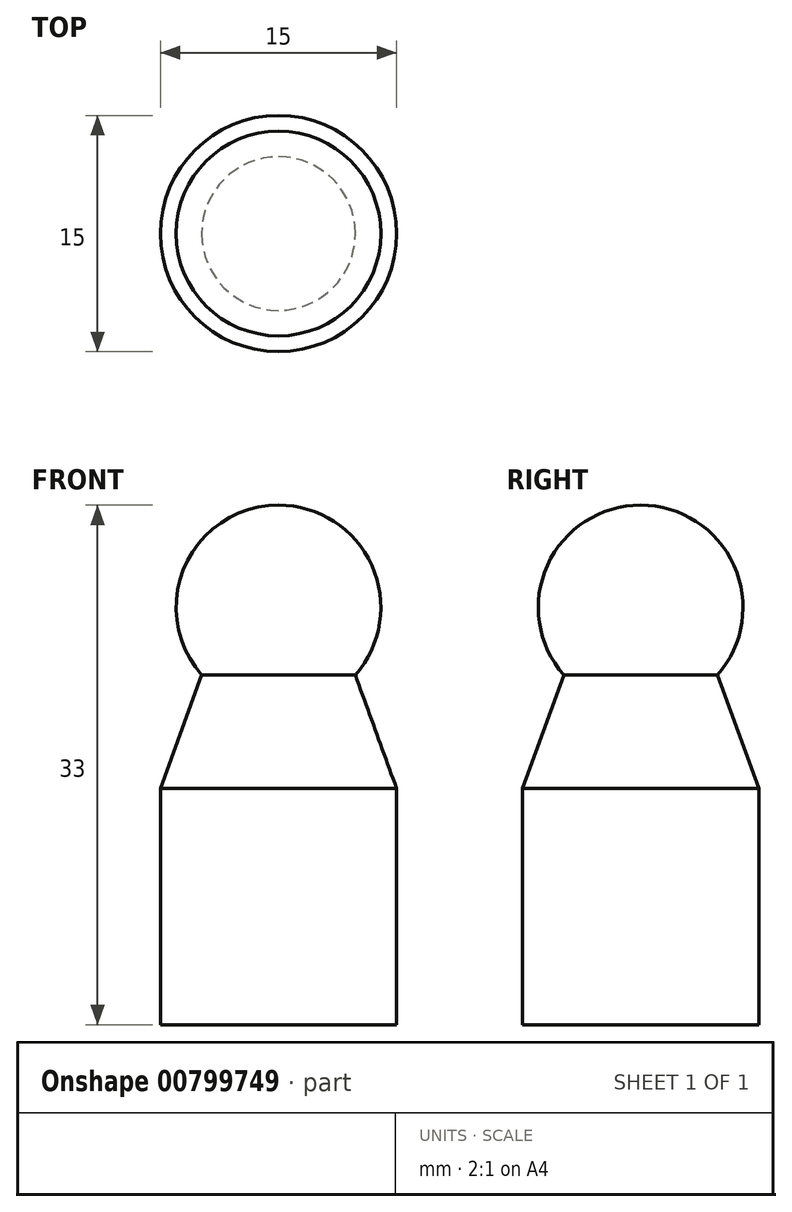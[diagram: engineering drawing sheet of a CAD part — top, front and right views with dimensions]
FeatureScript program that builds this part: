
annotation { "Feature Type Name" : "Feature", "Feature Type Description" : "" }
export const myFeature = defineFeature(function(context is Context, id is Id, definition is map)
    precondition{}
    {
        {
            var Q0;
            Q0=qCreatedBy(makeId("Top.planeOp"),FACE);
            var sketch = newSketch(context, id + "F0", { "sketchPlane" : qUnion([Q0])});
            skCircle(sketch, "E0", {"center": v(0, 0) * mm, "radius": 7.5 * mm});
            skSolve(sketch);
        }
        {
            var Q0;
            Q0=qSketchRegion(id+"F0",true);
            extrude(context, id + "F1", {"entities" : qUnion([Q0]), "depth" : 15 * mm, "offsetDistance" : 25 * mm});
        }
        {
            var Q0;
            Q0=makeQuery(id+"F1.opExtrude","CAP_FACE",FACE,{"disambiguationData":[OSD([sQuery(id+"F0.wireOp",EDGE,"E0")])],"isStart":false});
            var Q1;
            Q1 = qSketchRegion(id + "F3", true);
            extrude(context, id + "F2", {"entities" : qUnion([Q0, Q1]), "operationType" : NewBodyOperationType.ADD, "depth" : 10 * mm, "offsetDistance" : 25 * mm, "hasDraft" : true, "draftAngle" : 20 * degree, "draftPullDirection" : true});
        }
        {
            var Q0;
            Q0=qCreatedBy(makeId("Front.planeOp"),FACE);
            var sketch = newSketch(context, id + "F3", { "sketchPlane" : qUnion([Q0])});
            skArc(sketch, "E1", {"start": v(0, 20) * mm, "mid": v(6.5, 26.5) * mm, "end": v(0, 33) * mm});
            skLineSegment(sketch, "E2.0", {"start": v(-7.5, 15) * mm, "end": v(7.5, 15) * mm, "construction": true});
            skLineSegment(sketch, "E3", {"start": v(0, 20) * mm, "end": v(0, 33) * mm});
            skSolve(sketch);
        }
        {
            var Q0;
            Q0=qSketchRegion(id+"F3",true);
            var Q1;
            Q1=sQuery(id+"F3.wireOp",EDGE,"E3");
            revolve(context, id + "F4", {"operationType" : NewBodyOperationType.ADD, "entities" : qUnion([Q0]), "axis" : qUnion([Q1]), "revolveType" : RevolveType.FULL, "surfaceOperationType" : NewSurfaceOperationType.NEW});
        }
    });
